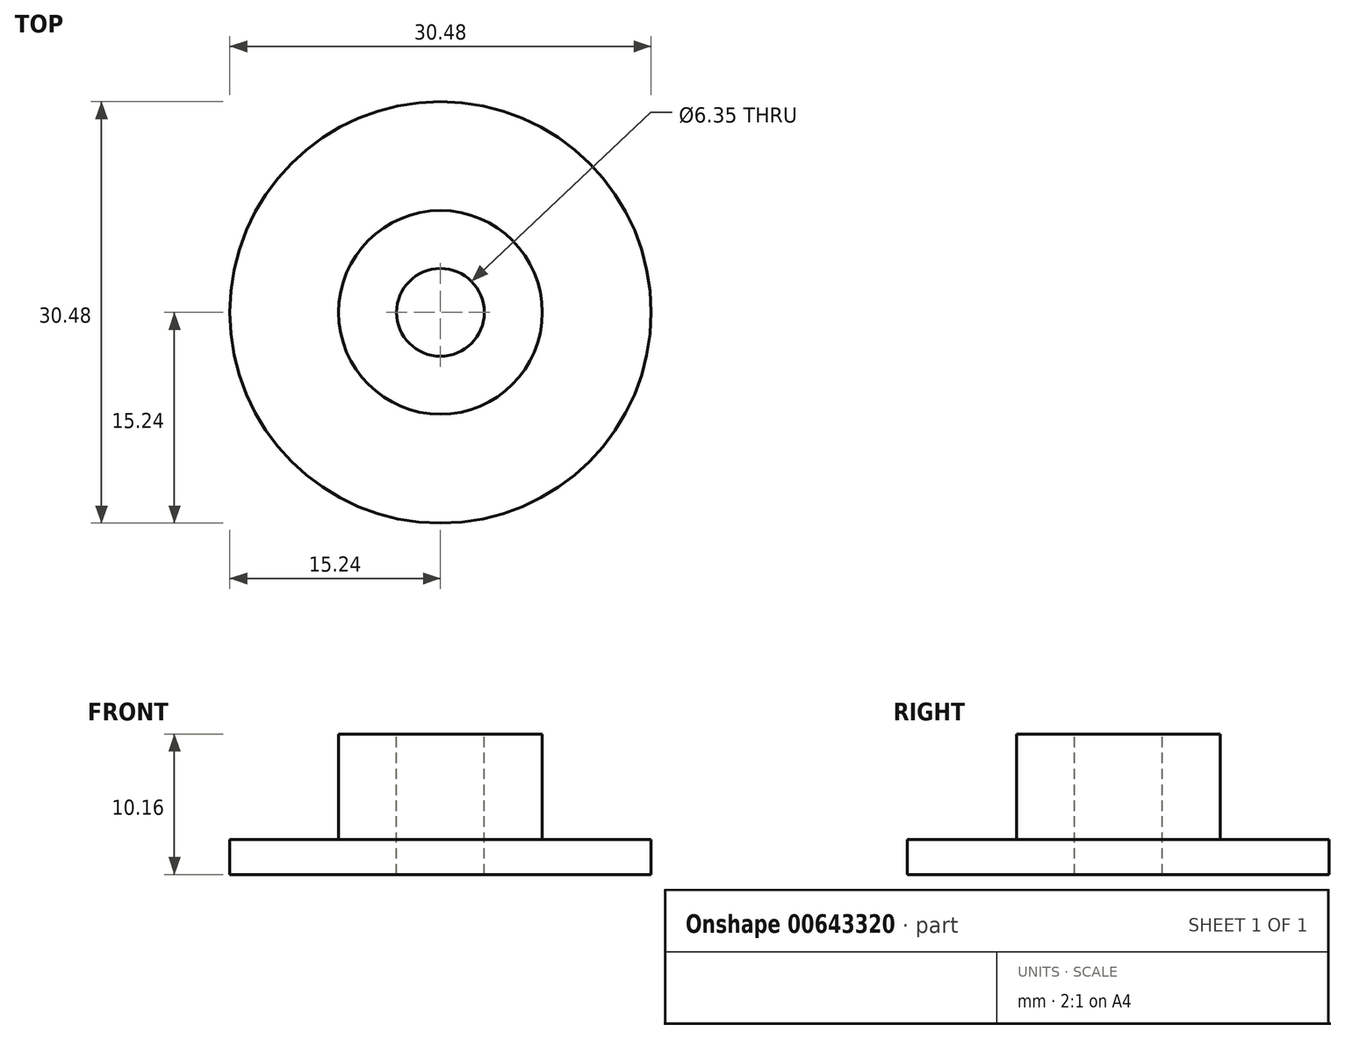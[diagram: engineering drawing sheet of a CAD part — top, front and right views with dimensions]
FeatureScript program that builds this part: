
annotation { "Feature Type Name" : "Feature", "Feature Type Description" : "" }
export const myFeature = defineFeature(function(context is Context, id is Id, definition is map)
    precondition{}
    {
        {
            var Q0;
            Q0=qCreatedBy(makeId("Top.planeOp"),FACE);
            var sketch = newSketch(context, id + "F0", { "sketchPlane" : qUnion([Q0])});
            skCircle(sketch, "E0", {"center": v(0, 0) * mm, "radius": 15.24 * mm});
            skCircle(sketch, "E1", {"center": v(0, 0) * mm, "radius": 7.37 * mm});
            skSolve(sketch);
        }
        {
            var Q0;
            Q0=makeQuery(id+"F0.imprint","IMPRINT",FACE,{"disambiguationData":[TD([[makeQuery(id+"F0.imprint","IMPRINT",EDGE,{"derivedFrom":sQuery(id+"F0.wireOp",EDGE,"E1")}),1.0]])]});
            var Q1;
            Q1=makeQuery(id+"F0.imprint","IMPRINT",FACE,{"disambiguationData":[TD([[makeQuery(id+"F0.imprint","IMPRINT",EDGE,{"derivedFrom":sQuery(id+"F0.wireOp",EDGE,"E0")}),1.0]])]});
            extrude(context, id + "F1", {"entities" : qUnion([Q0, Q1]), "depth" : 2.54 * mm, "offsetDistance" : 25.4 * mm});
        }
        {
            var Q0;
            Q0=makeQuery(id+"F1.opExtrude","CAP_FACE",FACE,{"disambiguationData":[OSD([sQuery(id+"F0.wireOp",EDGE,"E0")])],"isStart":false});
            var sketch = newSketch(context, id + "F2", { "sketchPlane" : qUnion([Q0])});
            skCircle(sketch, "E2.0", {"center": v(0, 0) * mm, "radius": 7.37 * mm});
            skSolve(sketch);
        }
        {
            var Q0;
            Q0=makeQuery(id+"F2.imprint","IMPRINT",FACE,{"disambiguationData":[TD([[makeQuery(id+"F2.imprint","IMPRINT",EDGE,{"derivedFrom":sQuery(id+"F2.wireOp",EDGE,"E2.0")}),1.0]])]});
            extrude(context, id + "F3", {"entities" : qUnion([Q0]), "operationType" : NewBodyOperationType.ADD, "depth" : 7.62 * mm, "offsetDistance" : 25.4 * mm});
        }
        {
            var Q0;
            Q0=makeQuery(id+"F3.opExtrude","CAP_FACE",FACE,{"disambiguationData":[OSD([sQuery(id+"F2.wireOp",EDGE,"E2.0")])],"isStart":false});
            var sketch = newSketch(context, id + "F4", { "sketchPlane" : qUnion([Q0])});
            skCircle(sketch, "E3", {"center": v(0, 0) * mm, "radius": 3.18 * mm});
            skSolve(sketch);
        }
        {
            var Q0;
            Q0=makeQuery(id+"F4.imprint","IMPRINT",FACE,{"disambiguationData":[TD([[makeQuery(id+"F4.imprint","IMPRINT",EDGE,{"derivedFrom":sQuery(id+"F4.wireOp",EDGE,"E3")}),1.0]])]});
            extrude(context, id + "F5", {"entities" : qUnion([Q0]), "operationType" : NewBodyOperationType.REMOVE, "oppositeDirection" : true, "depth" : 25.4 * mm, "offsetDistance" : 25.4 * mm});
        }
    });
